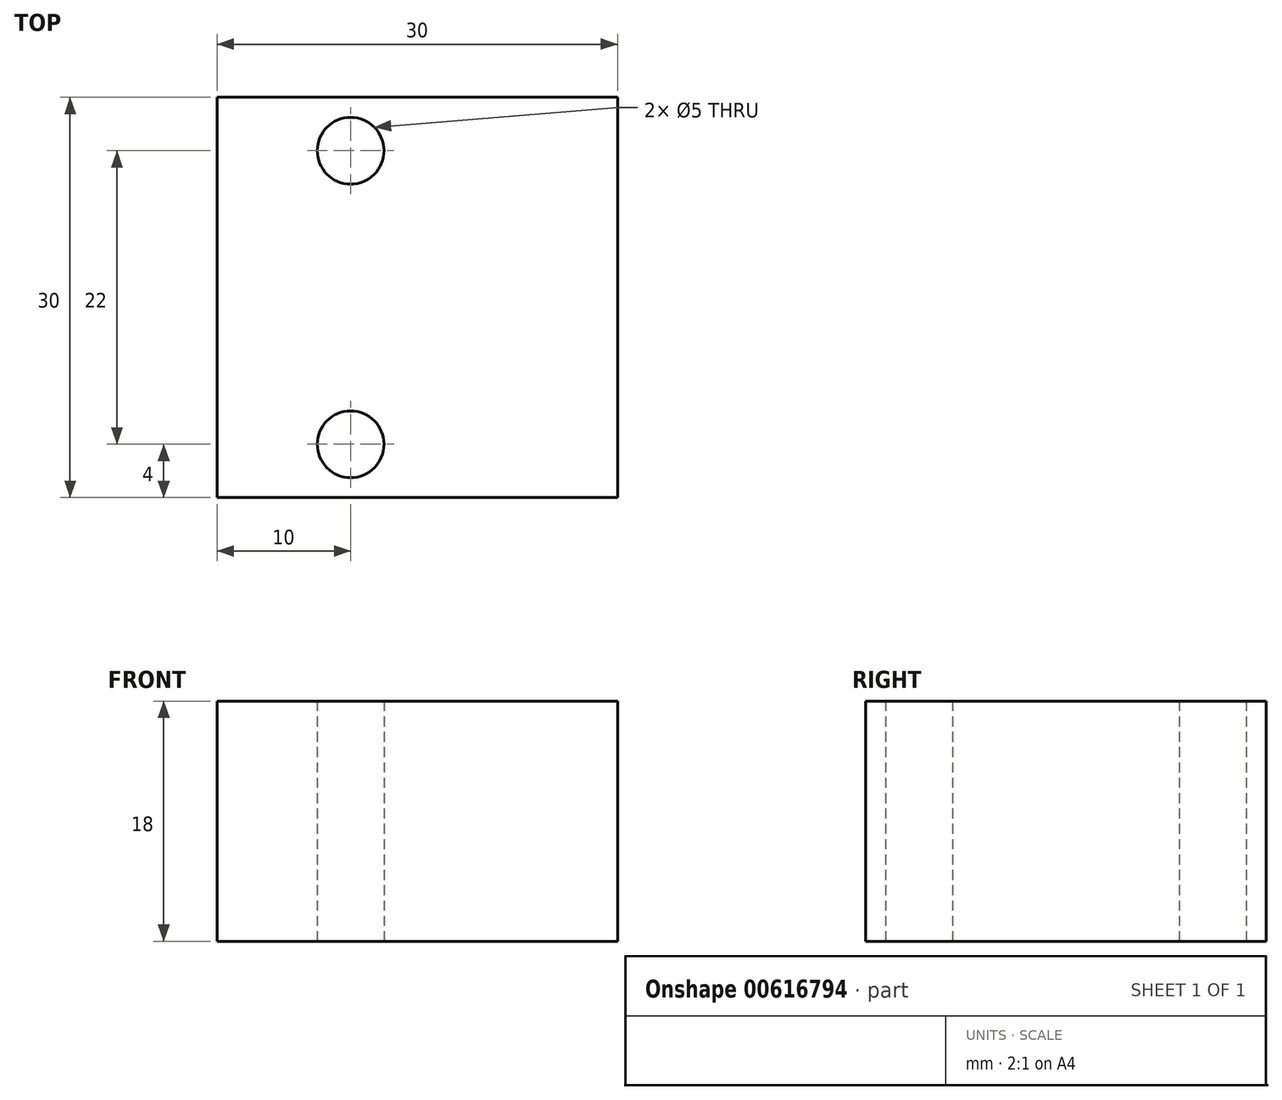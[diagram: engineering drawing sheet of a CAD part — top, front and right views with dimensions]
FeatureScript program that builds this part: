
annotation { "Feature Type Name" : "Feature", "Feature Type Description" : "" }
export const myFeature = defineFeature(function(context is Context, id is Id, definition is map)
    precondition{}
    {
        {
            var Q0;
            Q0=qCreatedBy(makeId("Top.planeOp"),FACE);
            var sketch = newSketch(context, id + "F0", { "sketchPlane" : qUnion([Q0])});
            skLineSegment(sketch, "E0.bottom", {"start": v(0, 0) * mm, "end": v(30, 0) * mm});
            skLineSegment(sketch, "E0.top", {"start": v(0, -30) * mm, "end": v(30, -30) * mm});
            skLineSegment(sketch, "E0.left", {"start": v(0, 0) * mm, "end": v(0, -30) * mm});
            skLineSegment(sketch, "E0.right", {"start": v(30, 0) * mm, "end": v(30, -30) * mm});
            skCircle(sketch, "E1", {"center": v(10, -4) * mm, "radius": 2.5 * mm});
            skCircle(sketch, "E2", {"center": v(10, -26) * mm, "radius": 2.5 * mm});
            skLineSegment(sketch, "E3", {"start": v(0, -15) * mm, "end": v(30, -15) * mm, "construction": true});
            skSolve(sketch);
        }
        {
            var Q0;
            Q0 = qSketchRegion(id + "F0", true);
            extrude(context, id + "F1", {"entities" : qUnion([Q0]), "depth" : 18 * mm, "offsetDistance" : 25 * mm});
        }
    });
